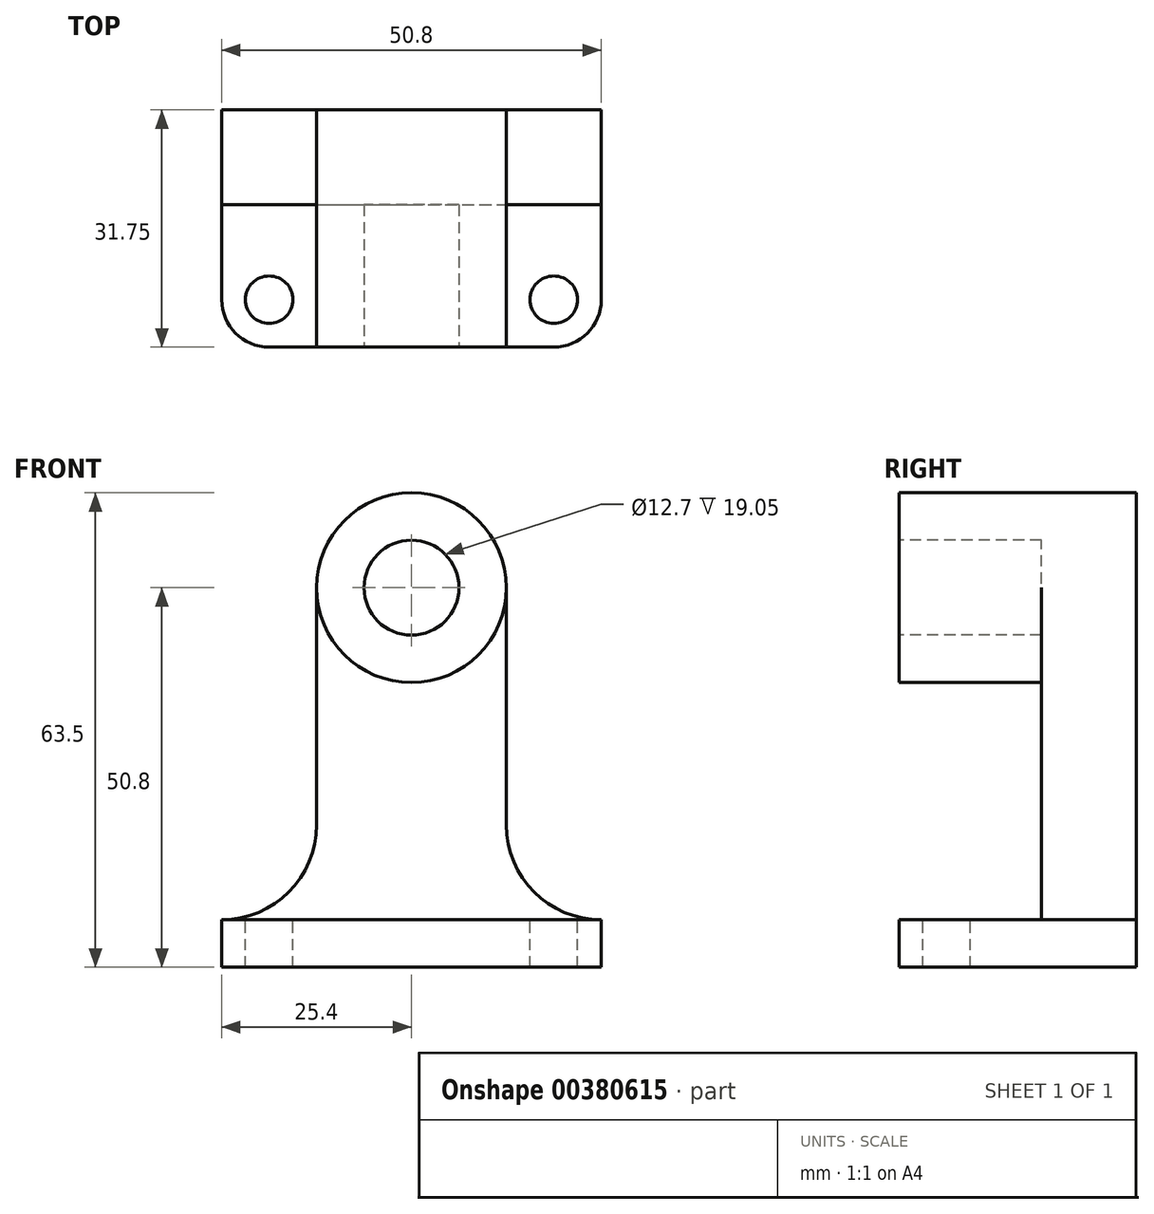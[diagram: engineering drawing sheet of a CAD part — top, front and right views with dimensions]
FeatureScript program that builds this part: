
annotation { "Feature Type Name" : "Feature", "Feature Type Description" : "" }
export const myFeature = defineFeature(function(context is Context, id is Id, definition is map)
    precondition{}
    {
        {
            var Q0;
            Q0=qCreatedBy(makeId("Front.planeOp"),FACE);
            var sketch = newSketch(context, id + "F0", { "sketchPlane" : qUnion([Q0])});
            skLineSegment(sketch, "E0.bottom", {"start": v(0, 0) * mm, "end": v(50.8, 0) * mm});
            skLineSegment(sketch, "E0.top", {"start": v(0, 63.5) * mm, "end": v(50.8, 63.5) * mm});
            skLineSegment(sketch, "E0.left", {"start": v(0, 0) * mm, "end": v(0, 63.5) * mm});
            skLineSegment(sketch, "E0.right", {"start": v(50.8, 0) * mm, "end": v(50.8, 63.5) * mm});
            skSolve(sketch);
        }
        {
            var Q0;
            Q0 = qSketchRegion(id + "F0", true);
            extrude(context, id + "F1", {"entities" : qUnion([Q0]), "depth" : 31.75 * mm});
        }
        {
            var Q0;
            Q0=makeQuery(id+"F1.opExtrude","CAP_FACE",FACE,{"disambiguationData":[OSD([sQuery(id+"F0.wireOp",EDGE,"E0.bottom"),sQuery(id+"F0.wireOp",EDGE,"E0.top"),sQuery(id+"F0.wireOp",EDGE,"E0.left"),sQuery(id+"F0.wireOp",EDGE,"E0.right")])],"isStart":false});
            var sketch = newSketch(context, id + "F2", { "sketchPlane" : qUnion([Q0])});
            skLineSegment(sketch, "E1", {"start": v(0, 6.35) * mm, "end": v(50.8, 6.35) * mm});
            skArc(sketch, "E2", {"start": v(0, 6.35) * mm, "mid": v(8.98, 10.07) * mm, "end": v(12.7, 19.05) * mm});
            skArc(sketch, "E3", {"start": v(38.1, 19.05) * mm, "mid": v(41.82, 10.07) * mm, "end": v(50.8, 6.35) * mm});
            skLineSegment(sketch, "E4", {"start": v(12.7, 50.8) * mm, "end": v(12.7, 19.05) * mm});
            skLineSegment(sketch, "E5", {"start": v(38.1, 19.05) * mm, "end": v(38.1, 50.8) * mm});
            skArc(sketch, "E6", {"start": v(38.1, 50.8) * mm, "mid": v(25.4, 63.5) * mm, "end": v(12.7, 50.8) * mm});
            skSolve(sketch);
        }
        {
            var Q0;
            {var subQ6=sQuery(id+"F2.wireOp",EDGE,"E2");Q0=makeQuery(id+"F2.imprint","IMPRINT",FACE,{"disambiguationData":[TD([[makeQuery(id+"F2.imprint","IMPRINT",EDGE,{"derivedFrom":subQ6}),1.0]])]});}
            var Q1;
            {var subQ6=sQuery(id+"F2.wireOp",EDGE,"E3");Q1=makeQuery(id+"F2.imprint","IMPRINT",FACE,{"disambiguationData":[TD([[makeQuery(id+"F2.imprint","IMPRINT",EDGE,{"derivedFrom":subQ6}),1.0]])]});}
            extrude(context, id + "F3", {"entities" : qUnion([Q0, Q1]), "operationType" : NewBodyOperationType.REMOVE, "oppositeDirection" : true, "depth" : 31.75 * mm});
        }
        {
            var Q0;
            Q0=makeQuery(id+"F1.opExtrude","CAP_FACE",FACE,{"disambiguationData":[OSD([sQuery(id+"F0.wireOp",EDGE,"E0.bottom"),sQuery(id+"F0.wireOp",EDGE,"E0.top"),sQuery(id+"F0.wireOp",EDGE,"E0.left"),sQuery(id+"F0.wireOp",EDGE,"E0.right")])],"isStart":false});
            var sketch = newSketch(context, id + "F4", { "sketchPlane" : qUnion([Q0])});
            skCircle(sketch, "E7", {"center": v(25.4, 50.8) * mm, "radius": 6.35 * mm});
            skCircle(sketch, "E8", {"center": v(25.4, 50.8) * mm, "radius": 12.7 * mm});
            skLineSegment(sketch, "E9", {"start": v(0, 6.35) * mm, "end": v(50.8, 6.35) * mm});
            skSolve(sketch);
        }
        {
            var Q0;
            Q0=makeQuery(id+"F4.imprint","IMPRINT",FACE,{"disambiguationData":[TD([[makeQuery(id+"F4.imprint","IMPRINT",EDGE,{"derivedFrom":sQuery(id+"F4.wireOp",EDGE,"E9")}),1.0]])]});
            var Q1;
            Q1=makeQuery(id+"F4.imprint","IMPRINT",FACE,{"disambiguationData":[TD([[makeQuery(id+"F4.imprint","IMPRINT",EDGE,{"derivedFrom":sQuery(id+"F4.wireOp",EDGE,"E7")}),1.0]])]});
            extrude(context, id + "F5", {"entities" : qUnion([Q0, Q1]), "operationType" : NewBodyOperationType.REMOVE, "oppositeDirection" : true, "depth" : 19.05 * mm});
        }
        {
            var Q0;
            Q0=makeQuery(id+"F5.boolean.opBoolean","COPY",FACE,{"derivedFrom":makeQuery(id+"F5.opExtrude","SWEPT_FACE",FACE,{"disambiguationData":[OSD([sQuery(id+"F4.wireOp",EDGE,"E9")])]})});
            var sketch = newSketch(context, id + "F6", { "sketchPlane" : qUnion([Q0])});
            skCircle(sketch, "E10", {"center": v(6.35, -25.4) * mm, "radius": 3.18 * mm});
            skCircle(sketch, "E11", {"center": v(44.45, -25.4) * mm, "radius": 3.17 * mm});
            skArc(sketch, "E12", {"start": v(0, -25.4) * mm, "mid": v(1.86, -29.9) * mm, "end": v(6.35, -31.75) * mm});
            skArc(sketch, "E13", {"start": v(44.45, -31.75) * mm, "mid": v(48.94, -29.9) * mm, "end": v(50.8, -25.4) * mm});
            skSolve(sketch);
        }
        {
            var Q0;
            Q0=makeQuery(id+"F6.imprint","IMPRINT",FACE,{"disambiguationData":[TD([[makeQuery(id+"F6.imprint","IMPRINT",EDGE,{"derivedFrom":sQuery(id+"F6.wireOp",EDGE,"E10")}),1.0]])]});
            var Q1;
            {var subQ0=sQuery(id+"F6.wireOp",EDGE,"E12");Q1=makeQuery(id+"F6.imprint","IMPRINT",FACE,{"disambiguationData":[TD([[makeQuery(id+"F6.imprint","IMPRINT",EDGE,{"derivedFrom":subQ0}),-1.0]])]});}
            var Q2;
            Q2=makeQuery(id+"F6.imprint","IMPRINT",FACE,{"disambiguationData":[TD([[makeQuery(id+"F6.imprint","IMPRINT",EDGE,{"derivedFrom":sQuery(id+"F6.wireOp",EDGE,"E11")}),1.0]])]});
            var Q3;
            {var subQ0=sQuery(id+"F6.wireOp",EDGE,"E13");Q3=makeQuery(id+"F6.imprint","IMPRINT",FACE,{"disambiguationData":[TD([[makeQuery(id+"F6.imprint","IMPRINT",EDGE,{"derivedFrom":subQ0}),-1.0]])]});}
            extrude(context, id + "F7", {"entities" : qUnion([Q0, Q1, Q2, Q3]), "operationType" : NewBodyOperationType.REMOVE, "oppositeDirection" : true, "depth" : 25.4 * mm});
        }
    });
